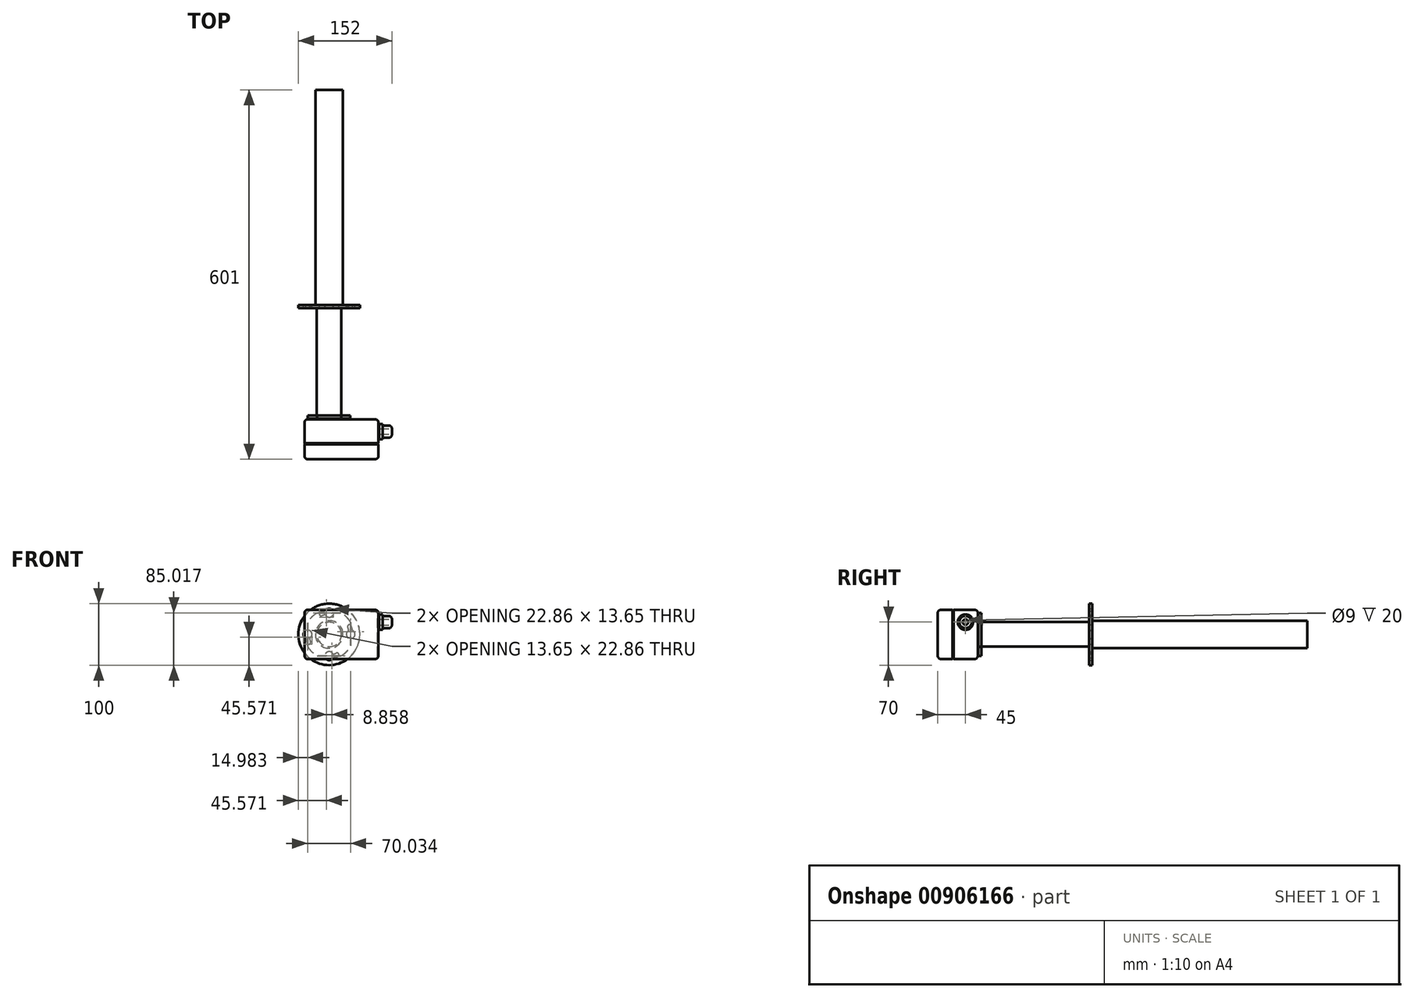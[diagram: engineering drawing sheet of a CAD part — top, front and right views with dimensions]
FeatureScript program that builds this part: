
annotation { "Feature Type Name" : "Feature", "Feature Type Description" : "" }
export const myFeature = defineFeature(function(context is Context, id is Id, definition is map)
    precondition{}
    {
        {
            var Q0;
            Q0=qCreatedBy(makeId("Front.planeOp"),FACE);
            var sketch = newSketch(context, id + "F0", { "sketchPlane" : qUnion([Q0])});
            skLineSegment(sketch, "E0.bottom", {"start": v(55, -40) * mm, "end": v(-55, -40) * mm});
            skLineSegment(sketch, "E0.top", {"start": v(55, 40) * mm, "end": v(-55, 40) * mm});
            skLineSegment(sketch, "E0.left", {"start": v(60, -35) * mm, "end": v(60, 35) * mm});
            skLineSegment(sketch, "E0.right", {"start": v(-60, -35) * mm, "end": v(-60, 35) * mm});
            skPoint(sketch, "E0.middle", {"position": v(0, 0) * mm});
            skPoint(sketch, "E1.visualSharp", {"position": v(-60, 40) * mm});
            skArc(sketch, "E1.filletArc", {"start": v(-55, 40) * mm, "mid": v(-58.54, 38.54) * mm, "end": v(-60, 35) * mm});
            skPoint(sketch, "E2.visualSharp", {"position": v(-60, -40) * mm});
            skArc(sketch, "E2.filletArc", {"start": v(-60, -35) * mm, "mid": v(-58.54, -38.54) * mm, "end": v(-55, -40) * mm});
            skPoint(sketch, "E3.visualSharp", {"position": v(60, 40) * mm});
            skArc(sketch, "E3.filletArc", {"start": v(60, 35) * mm, "mid": v(58.54, 38.54) * mm, "end": v(55, 40) * mm});
            skPoint(sketch, "E4.visualSharp", {"position": v(60, -40) * mm});
            skArc(sketch, "E4.filletArc", {"start": v(55, -40) * mm, "mid": v(58.54, -38.54) * mm, "end": v(60, -35) * mm});
            skSolve(sketch);
        }
        {
            var Q0;
            Q0=makeQuery(id+"F0.imprint","IMPRINT",FACE,{"disambiguationData":[TD([[makeQuery(id+"F0.imprint","IMPRINT",EDGE,{"derivedFrom":sQuery(id+"F0.wireOp",EDGE,"E0.bottom")}),-1.0]])]});
            extrude(context, id + "F1", {"entities" : qUnion([Q0]), "depth" : 40 * mm, "offsetDistance" : 25 * mm});
        }
        {
            var Q0;
            Q0=makeQuery(id+"F1.opExtrude","CAP_EDGE",EDGE,{"disambiguationData":[OSD([sQuery(id+"F0.wireOp",EDGE,"E0.bottom")])],"isStart":false});
            chamfer(context, id + "F2", {"entities" : qUnion([Q0]), "width" : 1 * mm, "tangentPropagation" : true});
        }
        {
            var Q0;
            Q0=makeQuery(id+"F1.opExtrude","CAP_FACE",FACE,{"disambiguationData":[OSD([sQuery(id+"F0.wireOp",EDGE,"E0.bottom"),sQuery(id+"F0.wireOp",EDGE,"E0.top"),sQuery(id+"F0.wireOp",EDGE,"E0.left"),sQuery(id+"F0.wireOp",EDGE,"E0.right"),sQuery(id+"F0.wireOp",EDGE,"E1.filletArc"),sQuery(id+"F0.wireOp",EDGE,"E2.filletArc"),sQuery(id+"F0.wireOp",EDGE,"E3.filletArc"),sQuery(id+"F0.wireOp",EDGE,"E4.filletArc")])],"isStart":true});
            fillet(context, id + "F3", {"entities" : qUnion([Q0]), "radius" : 5 * mm, "tangentPropagation" : true, "allowEdgeOverflow" : false});
        }
        {
            var Q0;
            Q0=makeQuery(id+"F1.opExtrude","CAP_FACE",FACE,{"disambiguationData":[OSD([sQuery(id+"F0.wireOp",EDGE,"E0.bottom"),sQuery(id+"F0.wireOp",EDGE,"E0.top"),sQuery(id+"F0.wireOp",EDGE,"E0.left"),sQuery(id+"F0.wireOp",EDGE,"E0.right"),sQuery(id+"F0.wireOp",EDGE,"E1.filletArc"),sQuery(id+"F0.wireOp",EDGE,"E2.filletArc"),sQuery(id+"F0.wireOp",EDGE,"E3.filletArc"),sQuery(id+"F0.wireOp",EDGE,"E4.filletArc")])],"isStart":false});
            var sketch = newSketch(context, id + "F4", { "sketchPlane" : qUnion([Q0])});
            skLineSegment(sketch, "E5.bottom", {"start": v(55, -40) * mm, "end": v(-55, -40) * mm});
            skLineSegment(sketch, "E5.top", {"start": v(55, 40) * mm, "end": v(-55, 40) * mm});
            skLineSegment(sketch, "E5.left", {"start": v(60, -35) * mm, "end": v(60, 35) * mm});
            skLineSegment(sketch, "E5.right", {"start": v(-60, -35) * mm, "end": v(-60, 35) * mm});
            skPoint(sketch, "E5.middle", {"position": v(0, 0) * mm});
            skPoint(sketch, "E6.visualSharp", {"position": v(-60, -40) * mm});
            skArc(sketch, "E6.filletArc", {"start": v(-60, -35) * mm, "mid": v(-58.54, -38.54) * mm, "end": v(-55, -40) * mm});
            skPoint(sketch, "E7.visualSharp", {"position": v(60, -40) * mm});
            skArc(sketch, "E7.filletArc", {"start": v(55, -40) * mm, "mid": v(58.54, -38.54) * mm, "end": v(60, -35) * mm});
            skPoint(sketch, "E8.visualSharp", {"position": v(60, 40) * mm});
            skArc(sketch, "E8.filletArc", {"start": v(60, 35) * mm, "mid": v(58.54, 38.54) * mm, "end": v(55, 40) * mm});
            skPoint(sketch, "E9.visualSharp", {"position": v(-60, 40) * mm});
            skArc(sketch, "E9.filletArc", {"start": v(-55, 40) * mm, "mid": v(-58.54, 38.54) * mm, "end": v(-60, 35) * mm});
            skSolve(sketch);
        }
        {
            var Q0;
            Q0=makeQuery(id+"F4.imprint","IMPRINT",FACE,{"disambiguationData":[TD([[makeQuery(id+"F4.imprint","IMPRINT",EDGE,{"derivedFrom":sQuery(id+"F4.wireOp",EDGE,"E5.bottom")}),-1.0]])]});
            var Q1;
            {var subQ0=sQuery(id+"F0.wireOp",EDGE,"E4.filletArc");var subQ1=sQuery(id+"F0.wireOp",EDGE,"E3.filletArc");var subQ2=sQuery(id+"F0.wireOp",EDGE,"E2.filletArc");var subQ3=sQuery(id+"F0.wireOp",EDGE,"E1.filletArc");var subQ4=sQuery(id+"F0.wireOp",EDGE,"E0.right");var subQ5=sQuery(id+"F0.wireOp",EDGE,"E0.left");var subQ6=sQuery(id+"F0.wireOp",EDGE,"E0.top");var subQ7=sQuery(id+"F0.wireOp",EDGE,"E0.bottom");var subQ8=makeQuery(id+"F1.opExtrude","CAP_FACE",FACE,{"disambiguationData":[OSD([subQ7,subQ6,subQ5,subQ4,subQ3,subQ2,subQ1,subQ0])],"isStart":false});Q1=makeQuery(id+"F4.imprint","IMPRINT",FACE,{"disambiguationData":[TD([[makeQuery(id+"F4.imprint","IMPRINT",EDGE,{"derivedFrom":makeQuery(id+"F2.opChamfer","BLEND_EDGE",EDGE,{"blendedFrom":[makeQuery(id+"F1.opExtrude","CAP_EDGE",EDGE,{"disambiguationData":[OSD([subQ7])],"isStart":false}),subQ8],"blendedInto":[subQ8]})}),1.0]])]});}
            extrude(context, id + "F5", {"entities" : qUnion([Q0, Q1]), "operationType" : NewBodyOperationType.ADD, "depth" : 25 * mm, "offsetDistance" : 25 * mm});
        }
        {
            var Q0;
            Q0=makeQuery(id+"F5.opExtrude","CAP_EDGE",EDGE,{"disambiguationData":[OSD([sQuery(id+"F4.wireOp",EDGE,"E5.top")])],"isStart":true});
            chamfer(context, id + "F6", {"entities" : qUnion([Q0]), "width" : 1 * mm, "tangentPropagation" : true});
        }
        {
            var Q0;
            Q0=makeQuery(id+"F1.opExtrude","SWEPT_BODY",BODY,{"disambiguationData":[OSD([sQuery(id+"F0.wireOp",EDGE,"E0.bottom"),sQuery(id+"F0.wireOp",EDGE,"E0.top"),sQuery(id+"F0.wireOp",EDGE,"E0.left"),sQuery(id+"F0.wireOp",EDGE,"E0.right"),sQuery(id+"F0.wireOp",EDGE,"E1.filletArc"),sQuery(id+"F0.wireOp",EDGE,"E2.filletArc"),sQuery(id+"F0.wireOp",EDGE,"E3.filletArc"),sQuery(id+"F0.wireOp",EDGE,"E4.filletArc")])]});
            transform(context, id + "F7", {"entities" : qUnion([Q0]), "transformType" : TransformType.TRANSLATION_3D, "dx" : 20 * mm, "dy" : 0 * mm, "dz" : 0 * mm, "makeCopy" : false});
        }
        {
            var Q0;
            Q0=makeQuery(id+"F5.opExtrude","CAP_FACE",FACE,{"disambiguationData":[OSD([sQuery(id+"F4.wireOp",EDGE,"E5.bottom"),sQuery(id+"F4.wireOp",EDGE,"E5.top"),sQuery(id+"F4.wireOp",EDGE,"E5.left"),sQuery(id+"F4.wireOp",EDGE,"E5.right"),sQuery(id+"F4.wireOp",EDGE,"E6.filletArc"),sQuery(id+"F4.wireOp",EDGE,"E7.filletArc"),sQuery(id+"F4.wireOp",EDGE,"E8.filletArc"),sQuery(id+"F4.wireOp",EDGE,"E9.filletArc")])],"isStart":false});
            fillet(context, id + "F8", {"entities" : qUnion([Q0]), "radius" : 5 * mm, "tangentPropagation" : true, "allowEdgeOverflow" : false});
        }
        {
            var Q0;
            Q0=makeQuery(id+"F1.opExtrude","SWEPT_FACE",FACE,{"disambiguationData":[OSD([sQuery(id+"F0.wireOp",EDGE,"E0.left")])]});
            cPlane(context, id + "F9", {"entities" : qUnion([Q0]), "cplaneType" : CPlaneType.OFFSET, "offset" : 1 * mm, "width" : 150 * mm, "height" : 150 * mm});
        }
        {
            var Q0;
            Q0=qCreatedBy(id+"F9.planeOp",FACE);
            var sketch = newSketch(context, id + "F10", { "sketchPlane" : qUnion([Q0])});
            skCircle(sketch, "E10", {"center": v(0, 0) * mm, "radius": 12.5 * mm});
            skSolve(sketch);
        }
        {
            var Q0;
            Q0=makeQuery(id+"F10.imprint","IMPRINT",FACE,{"disambiguationData":[TD([[makeQuery(id+"F10.imprint","IMPRINT",EDGE,{"derivedFrom":sQuery(id+"F10.wireOp",EDGE,"E10")}),1.0]])]});
            extrude(context, id + "F11", {"entities" : qUnion([Q0]), "depth" : 6 * mm, "offsetDistance" : 25 * mm});
        }
        {
            var Q0;
            Q0=makeQuery(id+"F11.opExtrude","CAP_FACE",FACE,{"disambiguationData":[OSD([sQuery(id+"F10.wireOp",EDGE,"E10")])],"isStart":false});
            var sketch = newSketch(context, id + "F12", { "sketchPlane" : qUnion([Q0])});
            skCircle(sketch, "E11", {"center": v(0, 0) * mm, "radius": 10 * mm});
            skSolve(sketch);
        }
        {
            var Q0;
            Q0=makeQuery(id+"F12.imprint","IMPRINT",FACE,{"disambiguationData":[TD([[makeQuery(id+"F12.imprint","IMPRINT",EDGE,{"derivedFrom":sQuery(id+"F12.wireOp",EDGE,"E11")}),1.0]])]});
            extrude(context, id + "F13", {"entities" : qUnion([Q0]), "operationType" : NewBodyOperationType.ADD, "depth" : 15 * mm, "offsetDistance" : 25 * mm});
        }
        {
            var Q0;
            Q0=makeQuery(id+"F13.opExtrude","CAP_EDGE",EDGE,{"disambiguationData":[OSD([sQuery(id+"F12.wireOp",EDGE,"E11")])],"isStart":false});
            fillet(context, id + "F14", {"entities" : qUnion([Q0]), "radius" : 5 * mm, "tangentPropagation" : true, "allowEdgeOverflow" : false});
        }
        {
            var Q0;
            Q0=makeQuery(id+"F13.opExtrude","CAP_FACE",FACE,{"disambiguationData":[OSD([sQuery(id+"F12.wireOp",EDGE,"E11")])],"isStart":false});
            var sketch = newSketch(context, id + "F15", { "sketchPlane" : qUnion([Q0])});
            skCircle(sketch, "E12", {"center": v(0, 0) * mm, "radius": 4.5 * mm});
            skSolve(sketch);
        }
        {
            var Q0;
            Q0=makeQuery(id+"F15.imprint","IMPRINT",FACE,{"disambiguationData":[TD([[makeQuery(id+"F15.imprint","IMPRINT",EDGE,{"derivedFrom":sQuery(id+"F15.wireOp",EDGE,"E12")}),1.0]])]});
            extrude(context, id + "F16", {"entities" : qUnion([Q0]), "operationType" : NewBodyOperationType.REMOVE, "oppositeDirection" : true, "depth" : 20 * mm, "offsetDistance" : 25 * mm});
        }
        {
            var Q0;
            Q0=makeQuery(id+"F11.opExtrude","SWEPT_BODY",BODY,{"disambiguationData":[OSD([sQuery(id+"F10.wireOp",EDGE,"E10")])]});
            transform(context, id + "F17", {"entities" : qUnion([Q0]), "transformType" : TransformType.TRANSLATION_3D, "dx" : 0 * mm, "dy" : -20 * mm, "dz" : 20 * mm, "makeCopy" : false});
        }
        {
            var Q0;
            Q0=makeQuery(id+"F1.opExtrude","CAP_FACE",FACE,{"disambiguationData":[OSD([sQuery(id+"F0.wireOp",EDGE,"E0.bottom"),sQuery(id+"F0.wireOp",EDGE,"E0.top"),sQuery(id+"F0.wireOp",EDGE,"E0.left"),sQuery(id+"F0.wireOp",EDGE,"E0.right"),sQuery(id+"F0.wireOp",EDGE,"E1.filletArc"),sQuery(id+"F0.wireOp",EDGE,"E2.filletArc"),sQuery(id+"F0.wireOp",EDGE,"E3.filletArc"),sQuery(id+"F0.wireOp",EDGE,"E4.filletArc")])],"isStart":true});
            var sketch = newSketch(context, id + "F18", { "sketchPlane" : qUnion([Q0])});
            skCircle(sketch, "E13", {"center": v(0, 0) * mm, "radius": 40 * mm});
            skLineSegment(sketch, "E14", {"start": v(35, 19.36) * mm, "end": v(35, -19.36) * mm});
            skLineSegment(sketch, "E15", {"start": v(19.36, -35) * mm, "end": v(-19.36, -35) * mm});
            skLineSegment(sketch, "E16", {"start": v(-19.36, 35) * mm, "end": v(19.36, 35) * mm});
            skLineSegment(sketch, "E17", {"start": v(-35, 19.36) * mm, "end": v(-35, -19.36) * mm});
            skSolve(sketch);
        }
        {
            var Q0;
            {var subQ0=sQuery(id+"F18.wireOp",EDGE,"E14");Q0=makeQuery(id+"F18.imprint","IMPRINT",FACE,{"disambiguationData":[TD([[makeQuery(id+"F18.imprint","IMPRINT",EDGE,{"derivedFrom":subQ0}),1.0]])]});}
            extrude(context, id + "F19", {"entities" : qUnion([Q0]), "operationType" : NewBodyOperationType.REMOVE, "oppositeDirection" : true, "depth" : 1 * mm, "offsetDistance" : 25 * mm});
        }
        {
            var Q0;
            Q0=makeQuery(id+"F19.boolean.opBoolean","COPY",FACE,{"derivedFrom":makeQuery(id+"F19.opExtrude","CAP_FACE",FACE,{"disambiguationData":[OSD([sQuery(id+"F18.wireOp",EDGE,"E13"),sQuery(id+"F18.wireOp",EDGE,"E14"),sQuery(id+"F18.wireOp",EDGE,"E15"),sQuery(id+"F18.wireOp",EDGE,"E16"),sQuery(id+"F18.wireOp",EDGE,"E17")])],"isStart":false})});
            cPlane(context, id + "F20", {"entities" : qUnion([Q0]), "cplaneType" : CPlaneType.OFFSET, "offset" : 2 * mm, "width" : 150 * mm, "height" : 150 * mm});
        }
        {
            var Q0;
            Q0=qCreatedBy(id+"F20.planeOp",FACE);
            var sketch = newSketch(context, id + "F21", { "sketchPlane" : qUnion([Q0])});
            skCircle(sketch, "E18", {"center": v(0, 0) * mm, "radius": 40 * mm});
            skLineSegment(sketch, "E19", {"start": v(35.05, 19.28) * mm, "end": v(35.05, -19.28) * mm});
            skLineSegment(sketch, "E20", {"start": v(19.77, 34.77) * mm, "end": v(-19.77, 34.77) * mm});
            skLineSegment(sketch, "E21", {"start": v(19.35, -35) * mm, "end": v(-19.35, -35) * mm});
            skLineSegment(sketch, "E22", {"start": v(-34.54, 20.17) * mm, "end": v(-34.54, -20.17) * mm});
            skSolve(sketch);
        }
        {
            var Q0;
            {var subQ0=sQuery(id+"F21.wireOp",EDGE,"E19");Q0=makeQuery(id+"F21.imprint","IMPRINT",FACE,{"disambiguationData":[TD([[makeQuery(id+"F21.imprint","IMPRINT",EDGE,{"derivedFrom":subQ0}),-1.0]])]});}
            extrude(context, id + "F22", {"entities" : qUnion([Q0]), "depth" : 5 * mm, "offsetDistance" : 25 * mm});
        }
        {
            var Q0;
            Q0=makeQuery(id+"F22.opExtrude","CAP_FACE",FACE,{"disambiguationData":[OSD([sQuery(id+"F21.wireOp",EDGE,"E18"),sQuery(id+"F21.wireOp",EDGE,"E19"),sQuery(id+"F21.wireOp",EDGE,"E20"),sQuery(id+"F21.wireOp",EDGE,"E21"),sQuery(id+"F21.wireOp",EDGE,"E22")])],"isStart":false});
            var sketch = newSketch(context, id + "F23", { "sketchPlane" : qUnion([Q0])});
            skCircle(sketch, "E23", {"center": v(0, 0) * mm, "radius": 20 * mm});
            skSolve(sketch);
        }
        {
            var Q0;
            Q0=makeQuery(id+"F23.imprint","IMPRINT",FACE,{"disambiguationData":[TD([[makeQuery(id+"F23.imprint","IMPRINT",EDGE,{"derivedFrom":sQuery(id+"F23.wireOp",EDGE,"E23")}),1.0]])]});
            extrude(context, id + "F24", {"entities" : qUnion([Q0]), "operationType" : NewBodyOperationType.ADD, "depth" : 180 * mm, "offsetDistance" : 25 * mm});
        }
        {
            var Q0;
            Q0=makeQuery(id+"F24.opExtrude","CAP_FACE",FACE,{"disambiguationData":[OSD([sQuery(id+"F23.wireOp",EDGE,"E23")])],"isStart":false});
            var sketch = newSketch(context, id + "F25", { "sketchPlane" : qUnion([Q0])});
            skCircle(sketch, "E24", {"center": v(0, 0) * mm, "radius": 50 * mm});
            skSolve(sketch);
        }
        {
            var Q0;
            Q0=makeQuery(id+"F25.imprint","IMPRINT",FACE,{"disambiguationData":[TD([[makeQuery(id+"F25.imprint","IMPRINT",EDGE,{"derivedFrom":sQuery(id+"F25.wireOp",EDGE,"E24")}),1.0]])]});
            extrude(context, id + "F26", {"entities" : qUnion([Q0]), "operationType" : NewBodyOperationType.ADD, "oppositeDirection" : true, "depth" : 5 * mm, "offsetDistance" : 25 * mm});
        }
        {
            var Q0;
            {var subQ0=sQuery(id+"F23.wireOp",EDGE,"E23");Q0=makeQuery(id+"F26.boolean.opBoolean","MERGE",FACE,{"derivedFrom":[makeQuery(id+"F24.opExtrude","CAP_FACE",FACE,{"disambiguationData":[OSD([subQ0])],"isStart":false}),makeQuery(id+"F26.opExtrude","CAP_FACE",FACE,{"disambiguationData":[OSD([subQ0,sQuery(id+"F25.wireOp",EDGE,"E24")])],"isStart":true})]});}
            var sketch = newSketch(context, id + "F27", { "sketchPlane" : qUnion([Q0])});
            skLineSegment(sketch, "E25", {"start": v(0, 0) * mm, "end": v(0, -35) * mm});
            skLineSegment(sketch, "E26", {"start": v(0, -35) * mm, "end": v(0, 35) * mm});
            skLineSegment(sketch, "E27", {"start": v(0, 0) * mm, "end": v(35, 0) * mm});
            skLineSegment(sketch, "E28", {"start": v(35, 0) * mm, "end": v(-35, 0) * mm});
            skSolve(sketch);
        }
        {
            var Q0;
            Q0=sQuery(id+"F27.wireOp",VERTEX,"E27.end");
            var Q1;
            Q1=sQuery(id+"F27.wireOp",VERTEX,"E25.end");
            var Q2;
            Q2=sQuery(id+"F27.wireOp",VERTEX,"E28.end");
            var Q3;
            Q3=sQuery(id+"F27.wireOp",VERTEX,"E26.end");
            var Q4;
            Q4=makeQuery(id+"F22.opExtrude","SWEPT_BODY",BODY,{"disambiguationData":[OSD([sQuery(id+"F21.wireOp",EDGE,"E18"),sQuery(id+"F21.wireOp",EDGE,"E19"),sQuery(id+"F21.wireOp",EDGE,"E20"),sQuery(id+"F21.wireOp",EDGE,"E21"),sQuery(id+"F21.wireOp",EDGE,"E22")])]});
            hole(context, id + "F28", {"style" : HoleStyle.SIMPLE, "endStyle" : HoleEndStyle.BLIND, "holeDiameter" : 14 * mm, "majorDiameter" : 5 * mm, "holeDepth" : 5 * mm, "isTappedThrough" : true, "tappedDepth" : 12 * mm, "tapClearance" : 3, "locations" : qUnion([Q0, Q1, Q2, Q3]), "scope" : qUnion([Q4])});
        }
        {
            var Q0;
            {var subQ0=sQuery(id+"F23.wireOp",EDGE,"E23");Q0=makeQuery(id+"F26.boolean.opBoolean","MERGE",FACE,{"derivedFrom":[makeQuery(id+"F24.opExtrude","CAP_FACE",FACE,{"disambiguationData":[OSD([subQ0])],"isStart":false}),makeQuery(id+"F26.opExtrude","CAP_FACE",FACE,{"disambiguationData":[OSD([subQ0,sQuery(id+"F25.wireOp",EDGE,"E24")])],"isStart":true})]});}
            var sketch = newSketch(context, id + "F29", { "sketchPlane" : qUnion([Q0])});
            skCircle(sketch, "E29", {"center": v(0, 0) * mm, "radius": 38.5 * mm});
            skCircle(sketch, "E30.0", {"center": v(0, 0) * mm, "radius": 32.5 * mm});
            skArc(sketch, "E31", {"start": v(30.3, -11.77) * mm, "mid": v(32, -15.66) * mm, "end": v(35.89, -13.95) * mm});
            skArc(sketch, "E32", {"start": v(-11.77, -30.3) * mm, "mid": v(-15.66, -32) * mm, "end": v(-13.95, -35.89) * mm});
            skArc(sketch, "E33", {"start": v(-30.3, 11.77) * mm, "mid": v(-32, 15.66) * mm, "end": v(-35.89, 13.95) * mm});
            skArc(sketch, "E34", {"start": v(11.77, 30.3) * mm, "mid": v(15.66, 32) * mm, "end": v(13.95, 35.89) * mm});
            skSolve(sketch);
        }
        {
            var Q0;
            {var subQ0=sQuery(id+"F29.wireOp",EDGE,"E31");Q0=makeQuery(id+"F29.imprint","IMPRINT",FACE,{"disambiguationData":[TD([[makeQuery(id+"F29.imprint","IMPRINT",EDGE,{"derivedFrom":subQ0}),1.0]])]});}
            var Q1;
            {var subQ0=sQuery(id+"F29.wireOp",EDGE,"E32");Q1=makeQuery(id+"F29.imprint","IMPRINT",FACE,{"disambiguationData":[TD([[makeQuery(id+"F29.imprint","IMPRINT",EDGE,{"derivedFrom":subQ0}),1.0]])]});}
            var Q2;
            {var subQ0=sQuery(id+"F29.wireOp",EDGE,"E33");Q2=makeQuery(id+"F29.imprint","IMPRINT",FACE,{"disambiguationData":[TD([[makeQuery(id+"F29.imprint","IMPRINT",EDGE,{"derivedFrom":subQ0}),1.0]])]});}
            var Q3;
            {var subQ0=sQuery(id+"F29.wireOp",EDGE,"E34");Q3=makeQuery(id+"F29.imprint","IMPRINT",FACE,{"disambiguationData":[TD([[makeQuery(id+"F29.imprint","IMPRINT",EDGE,{"derivedFrom":subQ0}),1.0]])]});}
            extrude(context, id + "F30", {"entities" : qUnion([Q0, Q1, Q2, Q3]), "operationType" : NewBodyOperationType.REMOVE, "oppositeDirection" : true, "depth" : 5 * mm, "offsetDistance" : 25 * mm});
        }
        {
            var Q0;
            {var subQ0=sQuery(id+"F23.wireOp",EDGE,"E23");Q0=makeQuery(id+"F26.boolean.opBoolean","MERGE",FACE,{"derivedFrom":[makeQuery(id+"F24.opExtrude","CAP_FACE",FACE,{"disambiguationData":[OSD([subQ0])],"isStart":false}),makeQuery(id+"F26.opExtrude","CAP_FACE",FACE,{"disambiguationData":[OSD([subQ0,sQuery(id+"F25.wireOp",EDGE,"E24")])],"isStart":true})]});}
            var sketch = newSketch(context, id + "F31", { "sketchPlane" : qUnion([Q0])});
            skCircle(sketch, "E35", {"center": v(0, 0) * mm, "radius": 22.5 * mm});
            skSolve(sketch);
        }
        {
            var Q0;
            Q0=makeQuery(id+"F31.imprint","IMPRINT",FACE,{"disambiguationData":[TD([[makeQuery(id+"F31.imprint","IMPRINT",EDGE,{"derivedFrom":sQuery(id+"F31.wireOp",EDGE,"E35")}),1.0]])]});
            extrude(context, id + "F32", {"entities" : qUnion([Q0]), "operationType" : NewBodyOperationType.ADD, "depth" : 350 * mm, "offsetDistance" : 25 * mm});
        }
    });
